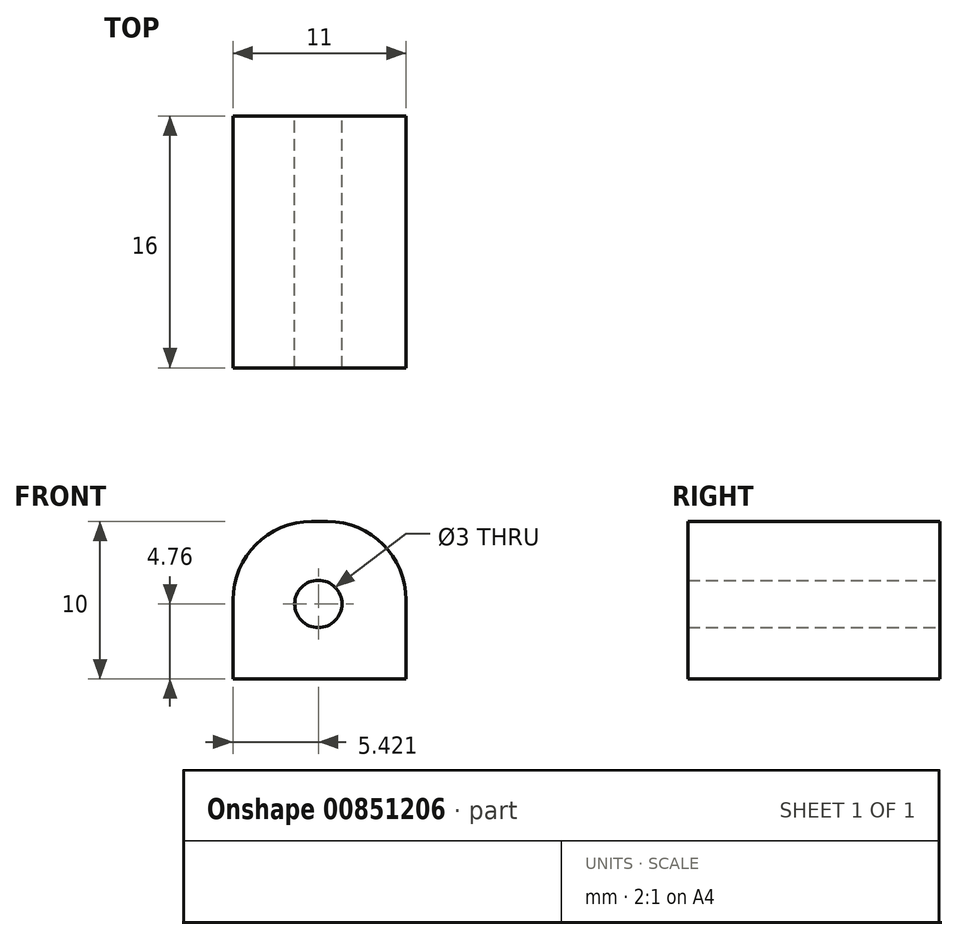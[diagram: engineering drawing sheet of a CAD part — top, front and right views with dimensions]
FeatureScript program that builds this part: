
annotation { "Feature Type Name" : "Feature", "Feature Type Description" : "" }
export const myFeature = defineFeature(function(context is Context, id is Id, definition is map)
    precondition{}
    {
        {
            var Q0;
            Q0=qCreatedBy(makeId("Front.planeOp"),FACE);
            var sketch = newSketch(context, id + "F0", { "sketchPlane" : qUnion([Q0])});
            skLineSegment(sketch, "E0.bottom", {"start": v(-9.62, 11.8) * mm, "end": v(-8.62, 11.8) * mm});
            skLineSegment(sketch, "E0.top", {"start": v(-14.62, 1.8) * mm, "end": v(-3.62, 1.8) * mm});
            skLineSegment(sketch, "E0.left", {"start": v(-14.62, 6.8) * mm, "end": v(-14.62, 1.8) * mm});
            skLineSegment(sketch, "E0.right", {"start": v(-3.62, 6.8) * mm, "end": v(-3.62, 1.8) * mm});
            skPoint(sketch, "E1.visualSharp", {"position": v(-14.62, 11.8) * mm});
            skArc(sketch, "E1.filletArc", {"start": v(-9.62, 11.8) * mm, "mid": v(-13.16, 10.34) * mm, "end": v(-14.62, 6.8) * mm});
            skPoint(sketch, "E2.visualSharp", {"position": v(-3.62, 11.8) * mm});
            skArc(sketch, "E2.filletArc", {"start": v(-3.62, 6.8) * mm, "mid": v(-5.09, 10.34) * mm, "end": v(-8.62, 11.8) * mm});
            skPoint(sketch, "E3", {"position": v(-4.74, 7.4) * mm});
            skPoint(sketch, "E4", {"position": v(-9.2, 6.57) * mm});
            skCircle(sketch, "E5", {"center": v(-9.2, 6.57) * mm, "radius": 1.5 * mm});
            skSolve(sketch);
        }
        {
            var Q0;
            Q0 = qSketchRegion(id + "F0", true);
            extrude(context, id + "F1", {"entities" : qUnion([Q0]), "depth" : 16 * mm, "offsetDistance" : 25 * mm});
        }
    });
